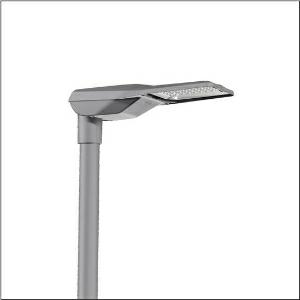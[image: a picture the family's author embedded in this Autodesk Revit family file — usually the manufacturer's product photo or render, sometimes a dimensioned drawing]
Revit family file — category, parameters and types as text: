
# Revit family: streetlight_sl_21_iq_mini___pl52_5xe2h41g08gb_5dc3
name_source: partatom
category: Lighting Fixtures
units: mm (PartAtom-declared; Revit-internal decimal feet)

## family parameters
Cut with Voids When Loaded = No
Host = Face
Light Source = No
Part Type = Normal
Room Calculation Point = No
Round Connector Dimension = Use Diameter
Shared = No

## types (1)
- --- (1 x LED, 5810 lm, 37.1 W, 4000K)
    Apparent Load = 37 VA
    CIE Flux Codes = 27 59 98 100 100
    Color Rendering = 70
    Color Temperature = 4000K
    Default Elevation = 1800 mm
    Description = Streetlight SL 21 mini, mast luminaire, primary light control with lens, of PMMA, primary optical cover: cover, of toughened safety glass, transparent, light distribution: PL52, light emission: direct distribution, primary light characteristic: asymmetric, installation type: post-top, side-entry, LED, High Power LED, rated luminous flux: 5.810lm, luminous efficacy: 157lm/W, light colour: 740, colour temperature: 4000K, control gear: ECG iQ, control: Street-Remote, Auto-Match, Temp-Guard, Lumen-Switch, Night-Set, Smart-Wire, Light-Fading, Desk-Remote (wireless, voltage-free reading and setting of iQ features in the workshop via application-optimized NFC function/RFID function), optimised constant luminous flux control (CLO 2.0), mains connection: 220..240V, AC, 50/60Hz, start of lifetime: 37W, end of lifetime: 39W, reduction: 18W, luminaire housing, of diecast aluminium, powder-coated, Siteco® metallic grey (DB 702S), corrosivity category C5 according to DIN EN ISO 12944, length: 628mm, width: 235mm, height: 110mm, spigot size: 60/76mm (post-top) and 42/60/76mm (side-entry), mast flange for spigot size: 42mm: 5XC10008XM4, 60mm: 5XC10008XM2, 76/60mm: 5XC10108XM1, protection rating (complete): IP66, insulation class (complete): insulation class II (safety insulation), certification: CE, ENEC, VDE, impact resistance: IK09, permissible operating ambient temperature for outdoor applications: -40..+50°C, standard-compliant lighting for roads and squares, packaging unit: 1 piece

Light Distribution: PL52
    Height = 110 mm
    Lamp = 1 x LED
    Lamp Light Flux = 5810 lm
    Lamp Power = 37.1 W
    Lamp count = 1
    Length = 625 mm
    Luminous efficacy = 157 lm/W
    Manufacturer = Siteco
    ModVariant = No
    Model = 5XE2H41G08GB
    Number of Poles = 1
    OnlyDefault = Yes
    Power Factor = 1
    Product Name = Streetlight SL 21 iQ mini | PL52
    Product group = mast luminaire | pylon top
    ProductGroupID = 6100
    Protection Class = Protection class II
    Protection Degree = IP 66
    RLX_Detail_Level = 1
    RlxData = <blob elided: 101997 chars, md5=4fd62dcc>
    Socket = socket
    Standby Power = 0 W
    System Light Flux = 5810 lm
    System Power = 37 W
    Type Comments = factory setting: luminous flux: 100 % | dim-lin: 254 | 385 mA
    Type Image = l_1003519.jpg
    URL = http://relux.com
    VarID = @adj_109455
    Voltage = 0 V
    Weight = 0.00 kg
    Width = 234 mm

## geometry (parser evidence)
native form markers: Blend x4, Sweep x11
no freeform markers — native parametric forms only
